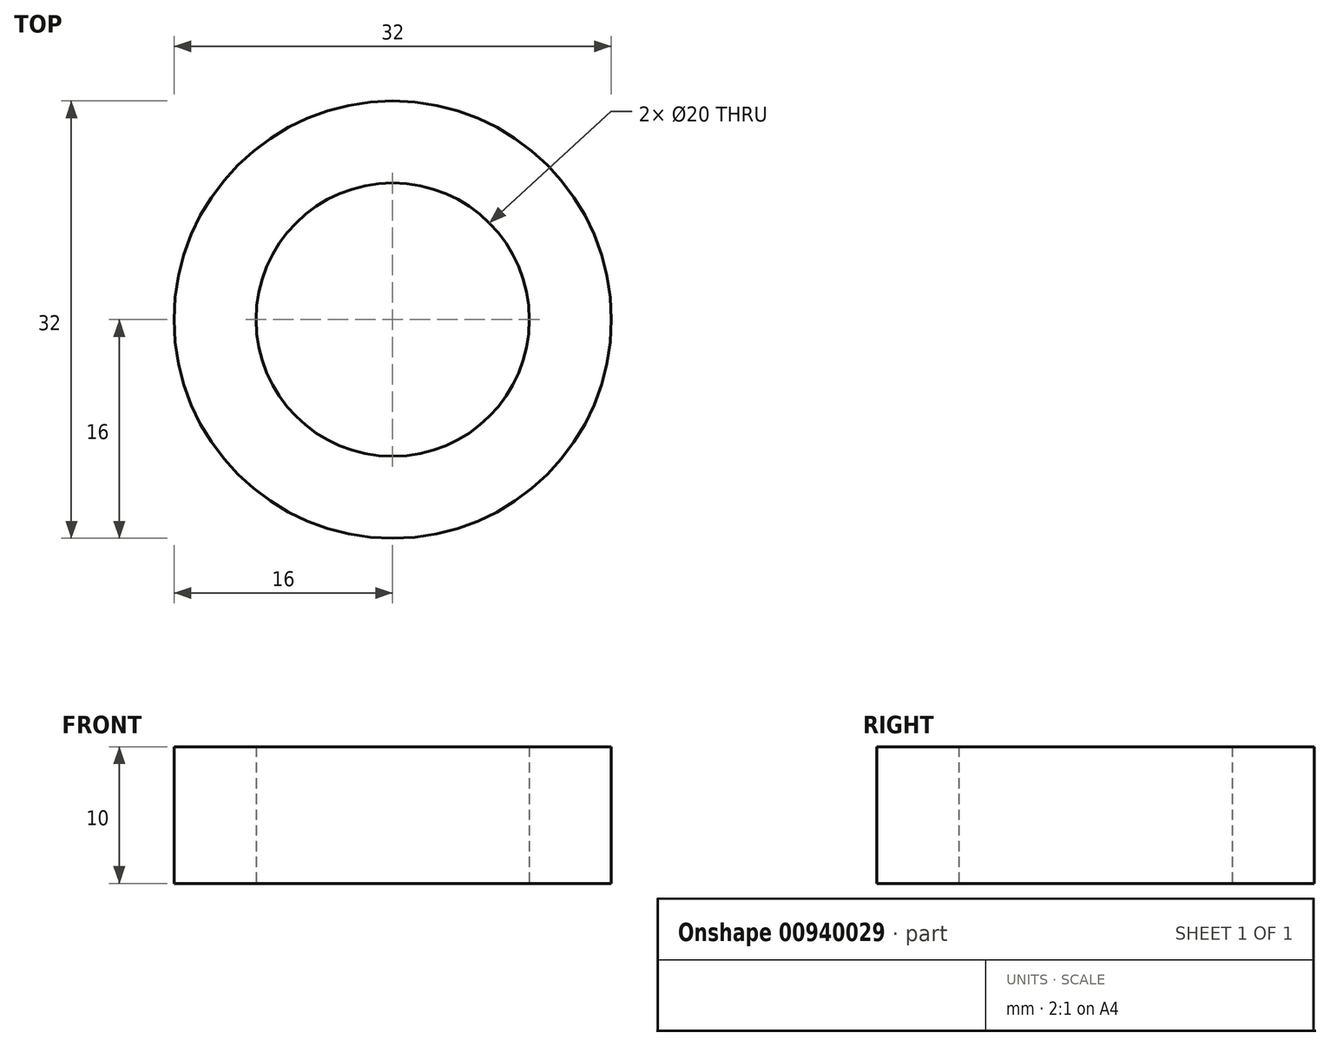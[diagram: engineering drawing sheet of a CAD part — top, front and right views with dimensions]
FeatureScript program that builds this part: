
annotation { "Feature Type Name" : "Feature", "Feature Type Description" : "" }
export const myFeature = defineFeature(function(context is Context, id is Id, definition is map)
    precondition{}
    {
        {
            var Q0;
            Q0=qCreatedBy(makeId("Top.planeOp"),FACE);
            var sketch = newSketch(context, id + "F0", { "sketchPlane" : qUnion([Q0])});
            skCircle(sketch, "E0", {"center": v(0, 0) * mm, "radius": 10 * mm});
            skCircle(sketch, "E1", {"center": v(0, 0) * mm, "radius": 16 * mm});
            skSolve(sketch);
        }
        {
            var Q0;
            Q0 = qSketchRegion(id + "F0", true);
            extrude(context, id + "F1", {"entities" : qUnion([Q0]), "depth" : 10 * mm, "offsetDistance" : 25 * mm});
        }
    });
